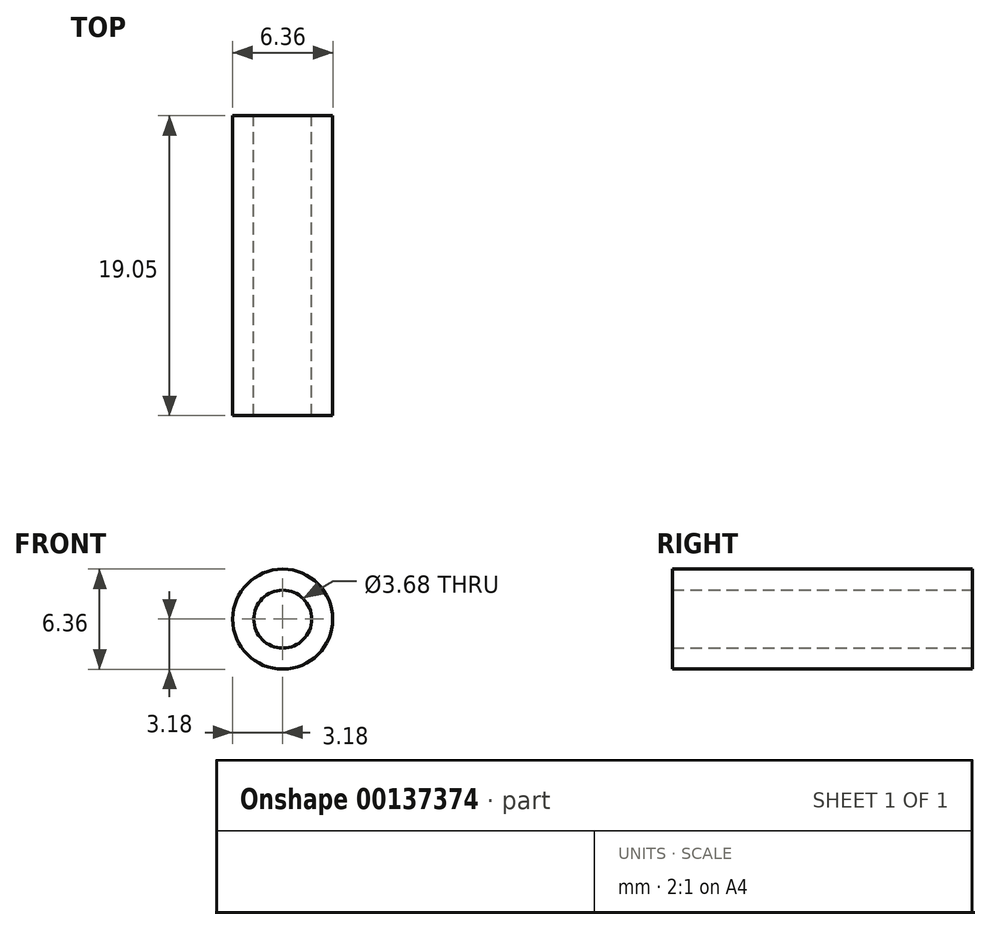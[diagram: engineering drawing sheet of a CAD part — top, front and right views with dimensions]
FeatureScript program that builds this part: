
annotation { "Feature Type Name" : "Feature", "Feature Type Description" : "" }
export const myFeature = defineFeature(function(context is Context, id is Id, definition is map)
    precondition{}
    {
        {
            var Q0;
            Q0=qCreatedBy(makeId("Front.planeOp"),FACE);
            var sketch = newSketch(context, id + "F0", { "sketchPlane" : qUnion([Q0])});
            skCircle(sketch, "E0", {"center": v(0, 0) * mm, "radius": 3.18 * mm});
            skCircle(sketch, "E1", {"center": v(0, 0) * mm, "radius": 1.84 * mm});
            skSolve(sketch);
        }
        {
            var Q0;
            Q0=makeQuery(id+"F0.imprint","IMPRINT",FACE,{"disambiguationData":[TD([[makeQuery(id+"F0.imprint","IMPRINT",EDGE,{"derivedFrom":sQuery(id+"F0.wireOp",EDGE,"E0")}),1.0]])]});
            extrude(context, id + "F1", {"entities" : qUnion([Q0]), "depth" : 19.05 * mm});
        }
    });
